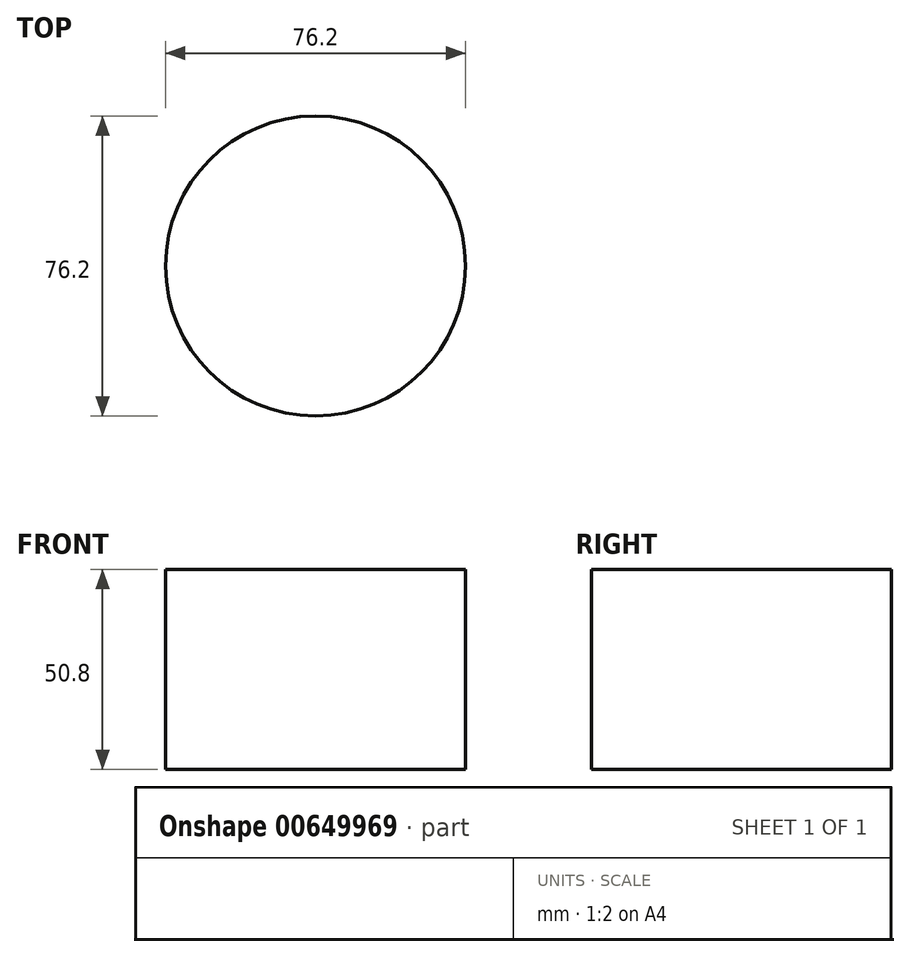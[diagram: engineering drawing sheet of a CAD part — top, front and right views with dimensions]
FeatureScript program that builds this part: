
annotation { "Feature Type Name" : "Feature", "Feature Type Description" : "" }
export const myFeature = defineFeature(function(context is Context, id is Id, definition is map)
    precondition{}
    {
        {
            var Q0;
            Q0=qCreatedBy(makeId("Top.planeOp"),FACE);
            var sketch = newSketch(context, id + "F0", { "sketchPlane" : qUnion([Q0])});
            skCircle(sketch, "E0", {"center": v(0, 0) * mm, "radius": 38.1 * mm});
            skSolve(sketch);
        }
        {
            var Q0;
            Q0 = qSketchRegion(id + "F0", true);
            extrude(context, id + "F1", {"entities" : qUnion([Q0]), "depth" : 50.8 * mm, "offsetDistance" : 25.4 * mm});
        }
        {
            var Q0;
            Q0=makeQuery(id+"F1.opExtrude","CAP_FACE",FACE,{"disambiguationData":[OSD([sQuery(id+"F0.wireOp",EDGE,"E0")])],"isStart":false});
            var sketch = newSketch(context, id + "F2", { "sketchPlane" : qUnion([Q0])});
            skFitSpline(sketch, "E1", {"points": [v(-29.33, -24.32) * mm, v(0, 0) * mm, v(-38.1, 0) * mm], "startDerivative": vector(92.35, 60.8) * mm, "endDerivative": vector(-109.9, -12.16) * mm});
            skSolve(sketch);
        }
        {
            var Q0;
            {var subQ0=sQuery(id+"F2.wireOp",EDGE,"E1");Q0=makeQuery(id+"F2.imprint","IMPRINT",FACE,{"disambiguationData":[TD([[makeQuery(id+"F2.imprint","IMPRINT",EDGE,{"derivedFrom":subQ0}),1.0]])]});}
            var Q1;
            Q1=sQuery(id+"F2.wireOp",EDGE,"E1");
            extrude(context, id + "F3", {"entities" : qUnion([Q0]), "bodyType" : ToolBodyType.SURFACE, "surfaceEntities" : qUnion([Q1]), "depth" : 2.54 * mm, "offsetDistance" : 25.4 * mm});
        }
        {
            var Q0;
            Q0=makeQuery(id+"F3.opExtrude","SWEPT_BODY",BODY,{"disambiguationData":[OSD([sQuery(id+"F2.wireOp",EDGE,"E1")])]});
            var Q1;
            Q1=qCreatedBy(makeId("Right.planeOp"),FACE);
            mirror(context, id + "F4", {"entities" : qUnion([Q0]), "mirrorPlane" : qUnion([Q1])});
        }
        {
            var Q0;
            Q0=makeQuery(id+"F4.opPattern","COPY",BODY,{"derivedFrom":makeQuery(id+"F3.opExtrude","SWEPT_BODY",BODY,{"disambiguationData":[OSD([sQuery(id+"F2.wireOp",EDGE,"E1")])]}),"instanceName":"1"});
            var Q1;
            Q1=qCreatedBy(makeId("Front.planeOp"),FACE);
            mirror(context, id + "F5", {"entities" : qUnion([Q0]), "mirrorPlane" : qUnion([Q1])});
        }
        {
            var Q0;
            Q0=makeQuery(id+"F5.opPattern","COPY",BODY,{"derivedFrom":makeQuery(id+"F4.opPattern","COPY",BODY,{"derivedFrom":makeQuery(id+"F3.opExtrude","SWEPT_BODY",BODY,{"disambiguationData":[OSD([sQuery(id+"F2.wireOp",EDGE,"E1")])]}),"instanceName":"1"}),"instanceName":"1"});
            var Q1;
            Q1=qCreatedBy(makeId("Right.planeOp"),FACE);
            mirror(context, id + "F6", {"entities" : qUnion([Q0]), "mirrorPlane" : qUnion([Q1])});
        }
    });
